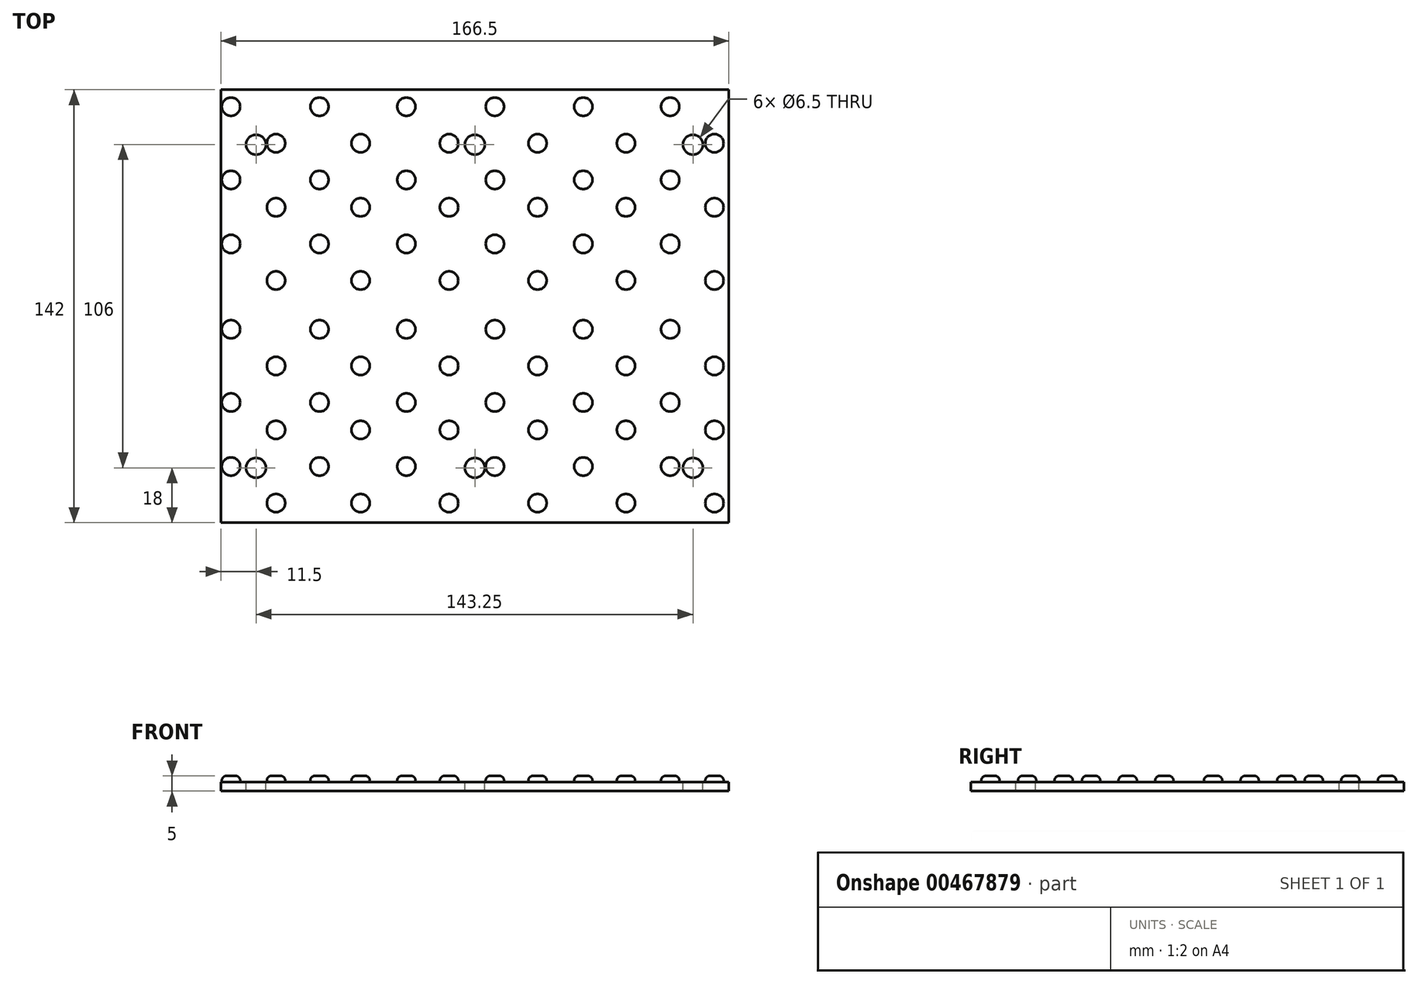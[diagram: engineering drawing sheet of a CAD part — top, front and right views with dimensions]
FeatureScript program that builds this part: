
annotation { "Feature Type Name" : "Feature", "Feature Type Description" : "" }
export const myFeature = defineFeature(function(context is Context, id is Id, definition is map)
    precondition{}
    {
        {
            var Q0;
            Q0=qCreatedBy(makeId("Top.planeOp"),FACE);
            var sketch = newSketch(context, id + "F0", { "sketchPlane" : qUnion([Q0])});
            skLineSegment(sketch, "E0.bottom", {"start": v(0, 0) * mm, "end": v(164.5, 0) * mm});
            skLineSegment(sketch, "E0.top", {"start": v(0, -138) * mm, "end": v(164.5, -138) * mm});
            skLineSegment(sketch, "E0.left", {"start": v(0, 0) * mm, "end": v(0, -138) * mm});
            skLineSegment(sketch, "E0.right", {"start": v(164.5, 0) * mm, "end": v(164.5, -138) * mm});
            skSolve(sketch);
        }
        {
            var Q0;
            Q0 = qSketchRegion(id + "F0", true);
            extrude(context, id + "F1", {"entities" : qUnion([Q0]), "depth" : 3 * mm, "offsetDistance" : 25 * mm});
        }
        {
            var Q0;
            Q0=makeQuery(id+"F1.opExtrude","CAP_FACE",FACE,{"disambiguationData":[OSD([sQuery(id+"F0.wireOp",EDGE,"E0.bottom"),sQuery(id+"F0.wireOp",EDGE,"E0.top"),sQuery(id+"F0.wireOp",EDGE,"E0.left"),sQuery(id+"F0.wireOp",EDGE,"E0.right")])],"isStart":false});
            var sketch = newSketch(context, id + "F2", { "sketchPlane" : qUnion([Q0])});
            skCircle(sketch, "E1", {"center": v(153.75, -122) * mm, "radius": 3.25 * mm});
            skCircle(sketch, "E2", {"center": v(153.75, -16) * mm, "radius": 3.25 * mm});
            skCircle(sketch, "E3", {"center": v(82.25, -16) * mm, "radius": 3.25 * mm});
            skCircle(sketch, "E4", {"center": v(10.5, -16) * mm, "radius": 3.25 * mm});
            skCircle(sketch, "E5", {"center": v(82.25, -122) * mm, "radius": 3.25 * mm});
            skCircle(sketch, "E6", {"center": v(10.5, -122) * mm, "radius": 3.25 * mm});
            skSolve(sketch);
        }
        {
            var Q0;
            Q0 = qSketchRegion(id + "F2", true);
            extrude(context, id + "F3", {"entities" : qUnion([Q0]), "operationType" : NewBodyOperationType.REMOVE, "oppositeDirection" : true, "depth" : 25 * mm, "offsetDistance" : 25 * mm});
        }
        {
            var Q0;
            Q0=makeQuery(id+"F1.opExtrude","SWEPT_FACE",FACE,{"disambiguationData":[OSD([sQuery(id+"F0.wireOp",EDGE,"E0.bottom")])]});
            extrude(context, id + "F4", {"entities" : qUnion([Q0]), "operationType" : NewBodyOperationType.ADD, "depth" : 2 * mm, "offsetDistance" : 25 * mm});
        }
        {
            var Q0;
            Q0=makeQuery(id+"F1.opExtrude","SWEPT_FACE",FACE,{"disambiguationData":[OSD([sQuery(id+"F0.wireOp",EDGE,"E0.top")])]});
            extrude(context, id + "F5", {"entities" : qUnion([Q0]), "operationType" : NewBodyOperationType.ADD, "depth" : 2 * mm, "offsetDistance" : 25 * mm});
        }
        {
            var Q0;
            {var subQ0=sQuery(id+"F0.wireOp",EDGE,"E0.right");Q0=makeQuery(id+"F5.boolean.opBoolean","MERGE",FACE,{"derivedFrom":[makeQuery(id+"F4.boolean.opBoolean","MERGE",FACE,{"derivedFrom":[makeQuery(id+"F1.opExtrude","SWEPT_FACE",FACE,{"disambiguationData":[OSD([subQ0])]}),makeQuery(id+"F4.opExtrude","SWEPT_FACE",FACE,{"disambiguationData":[OSD([sQuery(id+"F0.wireOp",EDGE,"E0.bottom"),subQ0])]})]}),makeQuery(id+"F5.opExtrude","SWEPT_FACE",FACE,{"disambiguationData":[OSD([sQuery(id+"F0.wireOp",EDGE,"E0.top"),subQ0])]})]});}
            extrude(context, id + "F6", {"entities" : qUnion([Q0]), "operationType" : NewBodyOperationType.ADD, "depth" : 1 * mm, "offsetDistance" : 25 * mm});
        }
        {
            var Q0;
            {var subQ0=sQuery(id+"F0.wireOp",EDGE,"E0.left");Q0=makeQuery(id+"F5.boolean.opBoolean","MERGE",FACE,{"derivedFrom":[makeQuery(id+"F4.boolean.opBoolean","MERGE",FACE,{"derivedFrom":[makeQuery(id+"F1.opExtrude","SWEPT_FACE",FACE,{"disambiguationData":[OSD([subQ0])]}),makeQuery(id+"F4.opExtrude","SWEPT_FACE",FACE,{"disambiguationData":[OSD([sQuery(id+"F0.wireOp",EDGE,"E0.bottom"),subQ0])]})]}),makeQuery(id+"F5.opExtrude","SWEPT_FACE",FACE,{"disambiguationData":[OSD([sQuery(id+"F0.wireOp",EDGE,"E0.top"),subQ0])]})]});}
            extrude(context, id + "F7", {"entities" : qUnion([Q0]), "operationType" : NewBodyOperationType.ADD, "depth" : 1 * mm, "offsetDistance" : 25 * mm});
        }
        {
            var Q0;
            {var subQ0=sQuery(id+"F0.wireOp",EDGE,"E0.left");var subQ1=sQuery(id+"F0.wireOp",EDGE,"E0.top");var subQ2=sQuery(id+"F0.wireOp",EDGE,"E0.bottom");var subQ3=sQuery(id+"F0.wireOp",EDGE,"E0.right");Q0=makeQuery(id+"F7.boolean.opBoolean","MERGE",FACE,{"derivedFrom":[makeQuery(id+"F6.boolean.opBoolean","MERGE",FACE,{"derivedFrom":[makeQuery(id+"F5.boolean.opBoolean","MERGE",FACE,{"derivedFrom":[makeQuery(id+"F4.boolean.opBoolean","MERGE",FACE,{"derivedFrom":[makeQuery(id+"F1.opExtrude","CAP_FACE",FACE,{"disambiguationData":[OSD([subQ2,subQ1,subQ0,subQ3])],"isStart":false}),makeQuery(id+"F4.opExtrude","SWEPT_FACE",FACE,{"disambiguationData":[OSD([subQ2]),TDD([makeQuery(id+"F1.opExtrude","CAP_EDGE",EDGE,{"disambiguationData":[OSD([subQ2])],"isStart":false})])]})]}),makeQuery(id+"F5.opExtrude","SWEPT_FACE",FACE,{"disambiguationData":[OSD([subQ1]),TDD([makeQuery(id+"F1.opExtrude","CAP_EDGE",EDGE,{"disambiguationData":[OSD([subQ1])],"isStart":false})])]})]}),makeQuery(id+"F6.opExtrude","SWEPT_FACE",FACE,{"disambiguationData":[OSD([subQ2,subQ1,subQ3]),TDD([makeQuery(id+"F5.boolean.opBoolean","MERGE",EDGE,{"derivedFrom":[makeQuery(id+"F4.boolean.opBoolean","MERGE",EDGE,{"derivedFrom":[makeQuery(id+"F1.opExtrude","CAP_EDGE",EDGE,{"disambiguationData":[OSD([subQ3])],"isStart":false}),makeQuery(id+"F4.opExtrude","SWEPT_EDGE",EDGE,{"disambiguationData":[OSD([subQ2,subQ3]),TDD([makeQuery(id+"F1.opExtrude","CAP_VERTEX",VERTEX,{"disambiguationData":[OSD([subQ2,subQ3])],"isStart":false})])]})]}),makeQuery(id+"F5.opExtrude","SWEPT_EDGE",EDGE,{"disambiguationData":[OSD([subQ1,subQ3]),TDD([makeQuery(id+"F1.opExtrude","CAP_VERTEX",VERTEX,{"disambiguationData":[OSD([subQ1,subQ3])],"isStart":false})])]})]})])]})]}),makeQuery(id+"F7.opExtrude","SWEPT_FACE",FACE,{"disambiguationData":[OSD([subQ2,subQ1,subQ0]),TDD([makeQuery(id+"F5.boolean.opBoolean","MERGE",EDGE,{"derivedFrom":[makeQuery(id+"F4.boolean.opBoolean","MERGE",EDGE,{"derivedFrom":[makeQuery(id+"F1.opExtrude","CAP_EDGE",EDGE,{"disambiguationData":[OSD([subQ0])],"isStart":false}),makeQuery(id+"F4.opExtrude","SWEPT_EDGE",EDGE,{"disambiguationData":[OSD([subQ2,subQ0]),TDD([makeQuery(id+"F1.opExtrude","CAP_VERTEX",VERTEX,{"disambiguationData":[OSD([subQ2,subQ0])],"isStart":false})])]})]}),makeQuery(id+"F5.opExtrude","SWEPT_EDGE",EDGE,{"disambiguationData":[OSD([subQ1,subQ0]),TDD([makeQuery(id+"F1.opExtrude","CAP_VERTEX",VERTEX,{"disambiguationData":[OSD([subQ1,subQ0])],"isStart":false})])]})]})])]})]});}
            var sketch = newSketch(context, id + "F8", { "sketchPlane" : qUnion([Q0])});
            skCircle(sketch, "E7", {"center": v(160.8, -133.56) * mm, "radius": 3 * mm});
            skCircle(sketch, "E8", {"center": v(131.8, -133.56) * mm, "radius": 3 * mm});
            skCircle(sketch, "E9", {"center": v(102.8, -133.56) * mm, "radius": 3 * mm});
            skCircle(sketch, "E10", {"center": v(73.8, -133.56) * mm, "radius": 3 * mm});
            skCircle(sketch, "E11", {"center": v(44.8, -133.56) * mm, "radius": 3 * mm});
            skCircle(sketch, "E12", {"center": v(17.05, -133.56) * mm, "radius": 3 * mm});
            skCircle(sketch, "E13", {"center": v(146.3, -121.56) * mm, "radius": 3 * mm});
            skCircle(sketch, "E14", {"center": v(117.8, -121.56) * mm, "radius": 3 * mm});
            skCircle(sketch, "E15", {"center": v(88.8, -121.56) * mm, "radius": 3 * mm});
            skCircle(sketch, "E16", {"center": v(59.8, -121.56) * mm, "radius": 3 * mm});
            skCircle(sketch, "E17", {"center": v(31.3, -121.56) * mm, "radius": 3 * mm});
            skCircle(sketch, "E18", {"center": v(2.3, -121.56) * mm, "radius": 3 * mm});
            skCircle(sketch, "E19", {"center": v(160.8, -109.56) * mm, "radius": 3 * mm});
            skCircle(sketch, "E20", {"center": v(131.8, -109.56) * mm, "radius": 3 * mm});
            skCircle(sketch, "E21", {"center": v(102.8, -109.56) * mm, "radius": 3 * mm});
            skCircle(sketch, "E22", {"center": v(73.8, -109.56) * mm, "radius": 3 * mm});
            skCircle(sketch, "E23", {"center": v(44.8, -109.56) * mm, "radius": 3 * mm});
            skCircle(sketch, "E24", {"center": v(17.05, -109.56) * mm, "radius": 3 * mm});
            skCircle(sketch, "E25", {"center": v(146.3, -100.56) * mm, "radius": 3 * mm});
            skCircle(sketch, "E26", {"center": v(117.8, -100.56) * mm, "radius": 3 * mm});
            skCircle(sketch, "E27", {"center": v(88.8, -100.56) * mm, "radius": 3 * mm});
            skCircle(sketch, "E28", {"center": v(59.8, -100.56) * mm, "radius": 3 * mm});
            skCircle(sketch, "E29", {"center": v(31.3, -100.56) * mm, "radius": 3 * mm});
            skCircle(sketch, "E30", {"center": v(2.3, -100.56) * mm, "radius": 3 * mm});
            skCircle(sketch, "E31", {"center": v(160.8, -88.56) * mm, "radius": 3 * mm});
            skCircle(sketch, "E32", {"center": v(131.8, -88.56) * mm, "radius": 3 * mm});
            skCircle(sketch, "E33", {"center": v(102.8, -88.56) * mm, "radius": 3 * mm});
            skCircle(sketch, "E34", {"center": v(73.8, -88.56) * mm, "radius": 3 * mm});
            skCircle(sketch, "E35", {"center": v(44.8, -88.56) * mm, "radius": 3 * mm});
            skCircle(sketch, "E36", {"center": v(17.05, -88.56) * mm, "radius": 3 * mm});
            skCircle(sketch, "E37", {"center": v(146.3, -76.56) * mm, "radius": 3 * mm});
            skCircle(sketch, "E38", {"center": v(117.8, -76.56) * mm, "radius": 3 * mm});
            skCircle(sketch, "E39", {"center": v(88.8, -76.56) * mm, "radius": 3 * mm});
            skCircle(sketch, "E40", {"center": v(59.8, -76.56) * mm, "radius": 3 * mm});
            skCircle(sketch, "E41", {"center": v(31.3, -76.56) * mm, "radius": 3 * mm});
            skCircle(sketch, "E42", {"center": v(2.3, -76.56) * mm, "radius": 3 * mm});
            skCircle(sketch, "E43", {"center": v(160.8, -60.56) * mm, "radius": 3 * mm});
            skCircle(sketch, "E44", {"center": v(131.8, -60.56) * mm, "radius": 3 * mm});
            skCircle(sketch, "E45", {"center": v(102.8, -60.56) * mm, "radius": 3 * mm});
            skCircle(sketch, "E46", {"center": v(73.8, -60.56) * mm, "radius": 3 * mm});
            skCircle(sketch, "E47", {"center": v(44.8, -60.56) * mm, "radius": 3 * mm});
            skCircle(sketch, "E48", {"center": v(17.05, -60.56) * mm, "radius": 3 * mm});
            skCircle(sketch, "E49", {"center": v(146.3, -48.56) * mm, "radius": 3 * mm});
            skCircle(sketch, "E50", {"center": v(117.8, -48.56) * mm, "radius": 3 * mm});
            skCircle(sketch, "E51", {"center": v(88.8, -48.56) * mm, "radius": 3 * mm});
            skCircle(sketch, "E52", {"center": v(59.8, -48.56) * mm, "radius": 3 * mm});
            skCircle(sketch, "E53", {"center": v(31.3, -48.56) * mm, "radius": 3 * mm});
            skCircle(sketch, "E54", {"center": v(2.3, -48.56) * mm, "radius": 3 * mm});
            skCircle(sketch, "E55", {"center": v(160.8, -36.56) * mm, "radius": 3 * mm});
            skCircle(sketch, "E56", {"center": v(131.8, -36.56) * mm, "radius": 3 * mm});
            skCircle(sketch, "E57", {"center": v(102.8, -36.56) * mm, "radius": 3 * mm});
            skCircle(sketch, "E58", {"center": v(73.8, -36.56) * mm, "radius": 3 * mm});
            skCircle(sketch, "E59", {"center": v(44.8, -36.56) * mm, "radius": 3 * mm});
            skCircle(sketch, "E60", {"center": v(17.05, -36.56) * mm, "radius": 3 * mm});
            skCircle(sketch, "E61", {"center": v(146.3, -27.56) * mm, "radius": 3 * mm});
            skCircle(sketch, "E62", {"center": v(117.8, -27.56) * mm, "radius": 3 * mm});
            skCircle(sketch, "E63", {"center": v(88.8, -27.56) * mm, "radius": 3 * mm});
            skCircle(sketch, "E64", {"center": v(59.8, -27.56) * mm, "radius": 3 * mm});
            skCircle(sketch, "E65", {"center": v(31.3, -27.56) * mm, "radius": 3 * mm});
            skCircle(sketch, "E66", {"center": v(2.3, -27.56) * mm, "radius": 3 * mm});
            skCircle(sketch, "E67", {"center": v(160.8, -15.56) * mm, "radius": 3 * mm});
            skCircle(sketch, "E68", {"center": v(131.8, -15.56) * mm, "radius": 3 * mm});
            skCircle(sketch, "E69", {"center": v(102.8, -15.56) * mm, "radius": 3 * mm});
            skCircle(sketch, "E70", {"center": v(73.8, -15.56) * mm, "radius": 3 * mm});
            skCircle(sketch, "E71", {"center": v(44.8, -15.56) * mm, "radius": 3 * mm});
            skCircle(sketch, "E72", {"center": v(17.05, -15.56) * mm, "radius": 3 * mm});
            skCircle(sketch, "E73", {"center": v(146.3, -3.56) * mm, "radius": 3 * mm});
            skCircle(sketch, "E74", {"center": v(117.8, -3.56) * mm, "radius": 3 * mm});
            skCircle(sketch, "E75", {"center": v(88.8, -3.56) * mm, "radius": 3 * mm});
            skCircle(sketch, "E76", {"center": v(59.8, -3.56) * mm, "radius": 3 * mm});
            skCircle(sketch, "E77", {"center": v(31.3, -3.56) * mm, "radius": 3 * mm});
            skCircle(sketch, "E78", {"center": v(2.3, -3.56) * mm, "radius": 3 * mm});
            skSolve(sketch);
        }
        {
            var Q0;
            Q0 = qSketchRegion(id + "F8", true);
            extrude(context, id + "F9", {"entities" : qUnion([Q0]), "operationType" : NewBodyOperationType.ADD, "depth" : 2 * mm, "offsetDistance" : 25 * mm});
        }
        {
            var Q0;
            Q0=makeQuery(id+"F9.opExtrude","CAP_EDGE",EDGE,{"disambiguationData":[OSD([sQuery(id+"F8.wireOp",EDGE,"E7")])],"isStart":false});
            var Q1;
            Q1=makeQuery(id+"F9.opExtrude","CAP_EDGE",EDGE,{"disambiguationData":[OSD([sQuery(id+"F8.wireOp",EDGE,"E19")])],"isStart":false});
            var Q2;
            Q2=makeQuery(id+"F9.opExtrude","CAP_EDGE",EDGE,{"disambiguationData":[OSD([sQuery(id+"F8.wireOp",EDGE,"E31")])],"isStart":false});
            var Q3;
            Q3=makeQuery(id+"F9.opExtrude","CAP_EDGE",EDGE,{"disambiguationData":[OSD([sQuery(id+"F8.wireOp",EDGE,"E25")])],"isStart":false});
            var Q4;
            Q4=makeQuery(id+"F9.opExtrude","CAP_EDGE",EDGE,{"disambiguationData":[OSD([sQuery(id+"F8.wireOp",EDGE,"E13")])],"isStart":false});
            var Q5;
            Q5=makeQuery(id+"F9.opExtrude","CAP_EDGE",EDGE,{"disambiguationData":[OSD([sQuery(id+"F8.wireOp",EDGE,"E8")])],"isStart":false});
            var Q6;
            Q6=makeQuery(id+"F9.opExtrude","CAP_EDGE",EDGE,{"disambiguationData":[OSD([sQuery(id+"F8.wireOp",EDGE,"E20")])],"isStart":false});
            var Q7;
            Q7=makeQuery(id+"F9.opExtrude","CAP_EDGE",EDGE,{"disambiguationData":[OSD([sQuery(id+"F8.wireOp",EDGE,"E32")])],"isStart":false});
            var Q8;
            Q8=makeQuery(id+"F9.opExtrude","CAP_EDGE",EDGE,{"disambiguationData":[OSD([sQuery(id+"F8.wireOp",EDGE,"E37")])],"isStart":false});
            var Q9;
            Q9=makeQuery(id+"F9.opExtrude","CAP_EDGE",EDGE,{"disambiguationData":[OSD([sQuery(id+"F8.wireOp",EDGE,"E44")])],"isStart":false});
            var Q10;
            Q10=makeQuery(id+"F9.opExtrude","CAP_EDGE",EDGE,{"disambiguationData":[OSD([sQuery(id+"F8.wireOp",EDGE,"E43")])],"isStart":false});
            var Q11;
            Q11=makeQuery(id+"F9.opExtrude","CAP_EDGE",EDGE,{"disambiguationData":[OSD([sQuery(id+"F8.wireOp",EDGE,"E49")])],"isStart":false});
            var Q12;
            Q12=makeQuery(id+"F9.opExtrude","CAP_EDGE",EDGE,{"disambiguationData":[OSD([sQuery(id+"F8.wireOp",EDGE,"E56")])],"isStart":false});
            var Q13;
            Q13=makeQuery(id+"F9.opExtrude","CAP_EDGE",EDGE,{"disambiguationData":[OSD([sQuery(id+"F8.wireOp",EDGE,"E61")])],"isStart":false});
            var Q14;
            Q14=makeQuery(id+"F9.opExtrude","CAP_EDGE",EDGE,{"disambiguationData":[OSD([sQuery(id+"F8.wireOp",EDGE,"E55")])],"isStart":false});
            var Q15;
            Q15=makeQuery(id+"F9.opExtrude","CAP_EDGE",EDGE,{"disambiguationData":[OSD([sQuery(id+"F8.wireOp",EDGE,"E67")])],"isStart":false});
            var Q16;
            Q16=makeQuery(id+"F9.opExtrude","CAP_EDGE",EDGE,{"disambiguationData":[OSD([sQuery(id+"F8.wireOp",EDGE,"E73")])],"isStart":false});
            var Q17;
            Q17=makeQuery(id+"F9.opExtrude","CAP_EDGE",EDGE,{"disambiguationData":[OSD([sQuery(id+"F8.wireOp",EDGE,"E68")])],"isStart":false});
            var Q18;
            Q18=makeQuery(id+"F9.opExtrude","CAP_EDGE",EDGE,{"disambiguationData":[OSD([sQuery(id+"F8.wireOp",EDGE,"E74")])],"isStart":false});
            var Q19;
            Q19=makeQuery(id+"F9.opExtrude","CAP_EDGE",EDGE,{"disambiguationData":[OSD([sQuery(id+"F8.wireOp",EDGE,"E62")])],"isStart":false});
            var Q20;
            Q20=makeQuery(id+"F9.opExtrude","CAP_EDGE",EDGE,{"disambiguationData":[OSD([sQuery(id+"F8.wireOp",EDGE,"E50")])],"isStart":false});
            var Q21;
            Q21=makeQuery(id+"F9.opExtrude","CAP_EDGE",EDGE,{"disambiguationData":[OSD([sQuery(id+"F8.wireOp",EDGE,"E38")])],"isStart":false});
            var Q22;
            Q22=makeQuery(id+"F9.opExtrude","CAP_EDGE",EDGE,{"disambiguationData":[OSD([sQuery(id+"F8.wireOp",EDGE,"E26")])],"isStart":false});
            var Q23;
            Q23=makeQuery(id+"F9.opExtrude","CAP_EDGE",EDGE,{"disambiguationData":[OSD([sQuery(id+"F8.wireOp",EDGE,"E14")])],"isStart":false});
            var Q24;
            Q24=makeQuery(id+"F9.opExtrude","CAP_EDGE",EDGE,{"disambiguationData":[OSD([sQuery(id+"F8.wireOp",EDGE,"E9")])],"isStart":false});
            var Q25;
            Q25=makeQuery(id+"F9.opExtrude","CAP_EDGE",EDGE,{"disambiguationData":[OSD([sQuery(id+"F8.wireOp",EDGE,"E21")])],"isStart":false});
            var Q26;
            Q26=makeQuery(id+"F9.opExtrude","CAP_EDGE",EDGE,{"disambiguationData":[OSD([sQuery(id+"F8.wireOp",EDGE,"E33")])],"isStart":false});
            var Q27;
            Q27=makeQuery(id+"F9.opExtrude","CAP_EDGE",EDGE,{"disambiguationData":[OSD([sQuery(id+"F8.wireOp",EDGE,"E45")])],"isStart":false});
            var Q28;
            Q28=makeQuery(id+"F9.opExtrude","CAP_EDGE",EDGE,{"disambiguationData":[OSD([sQuery(id+"F8.wireOp",EDGE,"E57")])],"isStart":false});
            var Q29;
            Q29=makeQuery(id+"F9.opExtrude","CAP_EDGE",EDGE,{"disambiguationData":[OSD([sQuery(id+"F8.wireOp",EDGE,"E69")])],"isStart":false});
            var Q30;
            Q30=makeQuery(id+"F9.opExtrude","CAP_EDGE",EDGE,{"disambiguationData":[OSD([sQuery(id+"F8.wireOp",EDGE,"E75")])],"isStart":false});
            var Q31;
            Q31=makeQuery(id+"F9.opExtrude","CAP_EDGE",EDGE,{"disambiguationData":[OSD([sQuery(id+"F8.wireOp",EDGE,"E63")])],"isStart":false});
            var Q32;
            Q32=makeQuery(id+"F9.opExtrude","CAP_EDGE",EDGE,{"disambiguationData":[OSD([sQuery(id+"F8.wireOp",EDGE,"E51")])],"isStart":false});
            var Q33;
            Q33=makeQuery(id+"F9.opExtrude","CAP_EDGE",EDGE,{"disambiguationData":[OSD([sQuery(id+"F8.wireOp",EDGE,"E39")])],"isStart":false});
            var Q34;
            Q34=makeQuery(id+"F9.opExtrude","CAP_EDGE",EDGE,{"disambiguationData":[OSD([sQuery(id+"F8.wireOp",EDGE,"E27")])],"isStart":false});
            var Q35;
            Q35=makeQuery(id+"F9.opExtrude","CAP_EDGE",EDGE,{"disambiguationData":[OSD([sQuery(id+"F8.wireOp",EDGE,"E15")])],"isStart":false});
            var Q36;
            Q36=makeQuery(id+"F9.opExtrude","CAP_EDGE",EDGE,{"disambiguationData":[OSD([sQuery(id+"F8.wireOp",EDGE,"E10")])],"isStart":false});
            var Q37;
            Q37=makeQuery(id+"F9.opExtrude","CAP_EDGE",EDGE,{"disambiguationData":[OSD([sQuery(id+"F8.wireOp",EDGE,"E22")])],"isStart":false});
            var Q38;
            Q38=makeQuery(id+"F9.opExtrude","CAP_EDGE",EDGE,{"disambiguationData":[OSD([sQuery(id+"F8.wireOp",EDGE,"E34")])],"isStart":false});
            var Q39;
            Q39=makeQuery(id+"F9.opExtrude","CAP_EDGE",EDGE,{"disambiguationData":[OSD([sQuery(id+"F8.wireOp",EDGE,"E46")])],"isStart":false});
            var Q40;
            Q40=makeQuery(id+"F9.opExtrude","CAP_EDGE",EDGE,{"disambiguationData":[OSD([sQuery(id+"F8.wireOp",EDGE,"E58")])],"isStart":false});
            var Q41;
            Q41=makeQuery(id+"F9.opExtrude","CAP_EDGE",EDGE,{"disambiguationData":[OSD([sQuery(id+"F8.wireOp",EDGE,"E70")])],"isStart":false});
            var Q42;
            Q42=makeQuery(id+"F9.opExtrude","CAP_EDGE",EDGE,{"disambiguationData":[OSD([sQuery(id+"F8.wireOp",EDGE,"E76")])],"isStart":false});
            var Q43;
            Q43=makeQuery(id+"F9.opExtrude","CAP_EDGE",EDGE,{"disambiguationData":[OSD([sQuery(id+"F8.wireOp",EDGE,"E64")])],"isStart":false});
            var Q44;
            Q44=makeQuery(id+"F9.opExtrude","CAP_EDGE",EDGE,{"disambiguationData":[OSD([sQuery(id+"F8.wireOp",EDGE,"E52")])],"isStart":false});
            var Q45;
            Q45=makeQuery(id+"F9.opExtrude","CAP_EDGE",EDGE,{"disambiguationData":[OSD([sQuery(id+"F8.wireOp",EDGE,"E40")])],"isStart":false});
            var Q46;
            Q46=makeQuery(id+"F9.opExtrude","CAP_EDGE",EDGE,{"disambiguationData":[OSD([sQuery(id+"F8.wireOp",EDGE,"E28")])],"isStart":false});
            var Q47;
            Q47=makeQuery(id+"F9.opExtrude","CAP_EDGE",EDGE,{"disambiguationData":[OSD([sQuery(id+"F8.wireOp",EDGE,"E16")])],"isStart":false});
            var Q48;
            Q48=makeQuery(id+"F9.opExtrude","CAP_EDGE",EDGE,{"disambiguationData":[OSD([sQuery(id+"F8.wireOp",EDGE,"E11")])],"isStart":false});
            var Q49;
            Q49=makeQuery(id+"F9.opExtrude","CAP_EDGE",EDGE,{"disambiguationData":[OSD([sQuery(id+"F8.wireOp",EDGE,"E23")])],"isStart":false});
            var Q50;
            Q50=makeQuery(id+"F9.opExtrude","CAP_EDGE",EDGE,{"disambiguationData":[OSD([sQuery(id+"F8.wireOp",EDGE,"E35")])],"isStart":false});
            var Q51;
            Q51=makeQuery(id+"F9.opExtrude","CAP_EDGE",EDGE,{"disambiguationData":[OSD([sQuery(id+"F8.wireOp",EDGE,"E47")])],"isStart":false});
            var Q52;
            Q52=makeQuery(id+"F9.opExtrude","CAP_EDGE",EDGE,{"disambiguationData":[OSD([sQuery(id+"F8.wireOp",EDGE,"E59")])],"isStart":false});
            var Q53;
            Q53=makeQuery(id+"F9.opExtrude","CAP_EDGE",EDGE,{"disambiguationData":[OSD([sQuery(id+"F8.wireOp",EDGE,"E71")])],"isStart":false});
            var Q54;
            Q54=makeQuery(id+"F9.opExtrude","CAP_EDGE",EDGE,{"disambiguationData":[OSD([sQuery(id+"F8.wireOp",EDGE,"E77")])],"isStart":false});
            var Q55;
            Q55=makeQuery(id+"F9.opExtrude","CAP_EDGE",EDGE,{"disambiguationData":[OSD([sQuery(id+"F8.wireOp",EDGE,"E65")])],"isStart":false});
            var Q56;
            Q56=makeQuery(id+"F9.opExtrude","CAP_EDGE",EDGE,{"disambiguationData":[OSD([sQuery(id+"F8.wireOp",EDGE,"E53")])],"isStart":false});
            var Q57;
            Q57=makeQuery(id+"F9.opExtrude","CAP_EDGE",EDGE,{"disambiguationData":[OSD([sQuery(id+"F8.wireOp",EDGE,"E41")])],"isStart":false});
            var Q58;
            Q58=makeQuery(id+"F9.opExtrude","CAP_EDGE",EDGE,{"disambiguationData":[OSD([sQuery(id+"F8.wireOp",EDGE,"E29")])],"isStart":false});
            var Q59;
            Q59=makeQuery(id+"F9.opExtrude","CAP_EDGE",EDGE,{"disambiguationData":[OSD([sQuery(id+"F8.wireOp",EDGE,"E17")])],"isStart":false});
            var Q60;
            Q60=makeQuery(id+"F9.opExtrude","CAP_EDGE",EDGE,{"disambiguationData":[OSD([sQuery(id+"F8.wireOp",EDGE,"E12")])],"isStart":false});
            var Q61;
            Q61=makeQuery(id+"F9.opExtrude","CAP_EDGE",EDGE,{"disambiguationData":[OSD([sQuery(id+"F8.wireOp",EDGE,"E24")])],"isStart":false});
            var Q62;
            Q62=makeQuery(id+"F9.opExtrude","CAP_EDGE",EDGE,{"disambiguationData":[OSD([sQuery(id+"F8.wireOp",EDGE,"E36")])],"isStart":false});
            var Q63;
            Q63=makeQuery(id+"F9.opExtrude","CAP_EDGE",EDGE,{"disambiguationData":[OSD([sQuery(id+"F8.wireOp",EDGE,"E48")])],"isStart":false});
            var Q64;
            Q64=makeQuery(id+"F9.opExtrude","CAP_EDGE",EDGE,{"disambiguationData":[OSD([sQuery(id+"F8.wireOp",EDGE,"E60")])],"isStart":false});
            var Q65;
            Q65=makeQuery(id+"F9.opExtrude","CAP_EDGE",EDGE,{"disambiguationData":[OSD([sQuery(id+"F8.wireOp",EDGE,"E72")])],"isStart":false});
            var Q66;
            Q66=makeQuery(id+"F9.opExtrude","CAP_EDGE",EDGE,{"disambiguationData":[OSD([sQuery(id+"F8.wireOp",EDGE,"E78")])],"isStart":false});
            var Q67;
            Q67=makeQuery(id+"F9.opExtrude","CAP_EDGE",EDGE,{"disambiguationData":[OSD([sQuery(id+"F8.wireOp",EDGE,"E54")])],"isStart":false});
            var Q68;
            Q68=makeQuery(id+"F9.opExtrude","CAP_EDGE",EDGE,{"disambiguationData":[OSD([sQuery(id+"F8.wireOp",EDGE,"E42")])],"isStart":false});
            var Q69;
            Q69=makeQuery(id+"F9.opExtrude","CAP_EDGE",EDGE,{"disambiguationData":[OSD([sQuery(id+"F8.wireOp",EDGE,"E66")])],"isStart":false});
            var Q70;
            Q70=makeQuery(id+"F9.opExtrude","CAP_EDGE",EDGE,{"disambiguationData":[OSD([sQuery(id+"F8.wireOp",EDGE,"E30")])],"isStart":false});
            var Q71;
            Q71=makeQuery(id+"F9.opExtrude","CAP_EDGE",EDGE,{"disambiguationData":[OSD([sQuery(id+"F8.wireOp",EDGE,"E18")])],"isStart":false});
            fillet(context, id + "F10", {"entities" : qUnion([Q0, Q1, Q2, Q3, Q4, Q5, Q6, Q7, Q8, Q9, Q10, Q11, Q12, Q13, Q14, Q15, Q16, Q17, Q18, Q19, Q20, Q21, Q22, Q23, Q24, Q25, Q26, Q27, Q28, Q29, Q30, Q31, Q32, Q33, Q34, Q35, Q36, Q37, Q38, Q39, Q40, Q41, Q42, Q43, Q44, Q45, Q46, Q47, Q48, Q49, Q50, Q51, Q52, Q53, Q54, Q55, Q56, Q57, Q58, Q59, Q60, Q61, Q62, Q63, Q64, Q65, Q66, Q67, Q68, Q69, Q70, Q71]), "tangentPropagation" : true, "radius" : 1.5 * mm, "defaultsChanged" : false, "vertexSettings" : [], "allowEdgeOverflow" : false});
        }
    });
